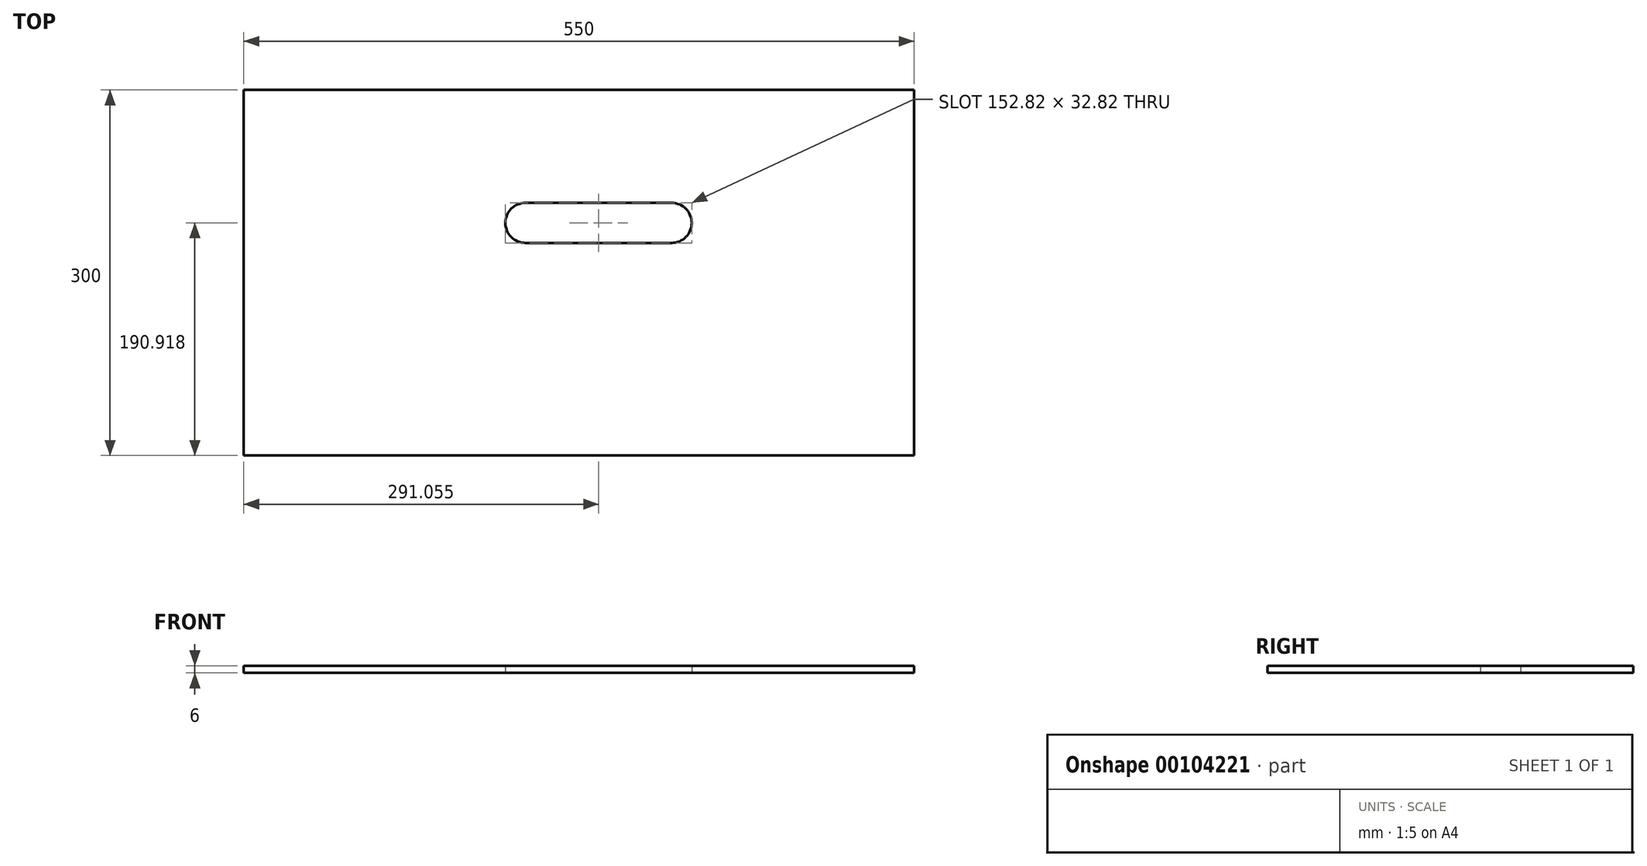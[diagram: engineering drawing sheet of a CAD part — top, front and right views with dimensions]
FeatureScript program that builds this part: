
annotation { "Feature Type Name" : "Feature", "Feature Type Description" : "" }
export const myFeature = defineFeature(function(context is Context, id is Id, definition is map)
    precondition{}
    {
        {
            var Q0;
            Q0=qCreatedBy(makeId("Top.planeOp"),FACE);
            var sketch = newSketch(context, id + "F0", { "sketchPlane" : qUnion([Q0])});
            skLineSegment(sketch, "E0.bottom", {"start": v(0, 0) * mm, "end": v(550, 0) * mm});
            skLineSegment(sketch, "E0.top", {"start": v(0, -300) * mm, "end": v(550, -300) * mm});
            skLineSegment(sketch, "E0.left", {"start": v(0, 0) * mm, "end": v(0, -300) * mm});
            skLineSegment(sketch, "E0.right", {"start": v(550, 0) * mm, "end": v(550, -300) * mm});
            skLineSegment(sketch, "E1.bottom", {"start": v(231.05, -92.67) * mm, "end": v(351.05, -92.67) * mm});
            skLineSegment(sketch, "E1.top", {"start": v(231.05, -125.5) * mm, "end": v(351.05, -125.5) * mm});
            skArc(sketch, "E2", {"start": v(231.05, -92.67) * mm, "mid": v(214.64, -109.08) * mm, "end": v(231.05, -125.5) * mm});
            skArc(sketch, "E3", {"start": v(351.05, -125.5) * mm, "mid": v(367.47, -109.08) * mm, "end": v(351.05, -92.67) * mm});
            skSolve(sketch);
        }
        {
            var Q0;
            Q0=makeQuery(id+"F0.imprint","IMPRINT",FACE,{"disambiguationData":[TD([[makeQuery(id+"F0.imprint","IMPRINT",EDGE,{"derivedFrom":sQuery(id+"F0.wireOp",EDGE,"E0.bottom")}),-1.0]])]});
            extrude(context, id + "F1", {"entities" : qUnion([Q0]), "depth" : 6 * mm});
        }
    });
